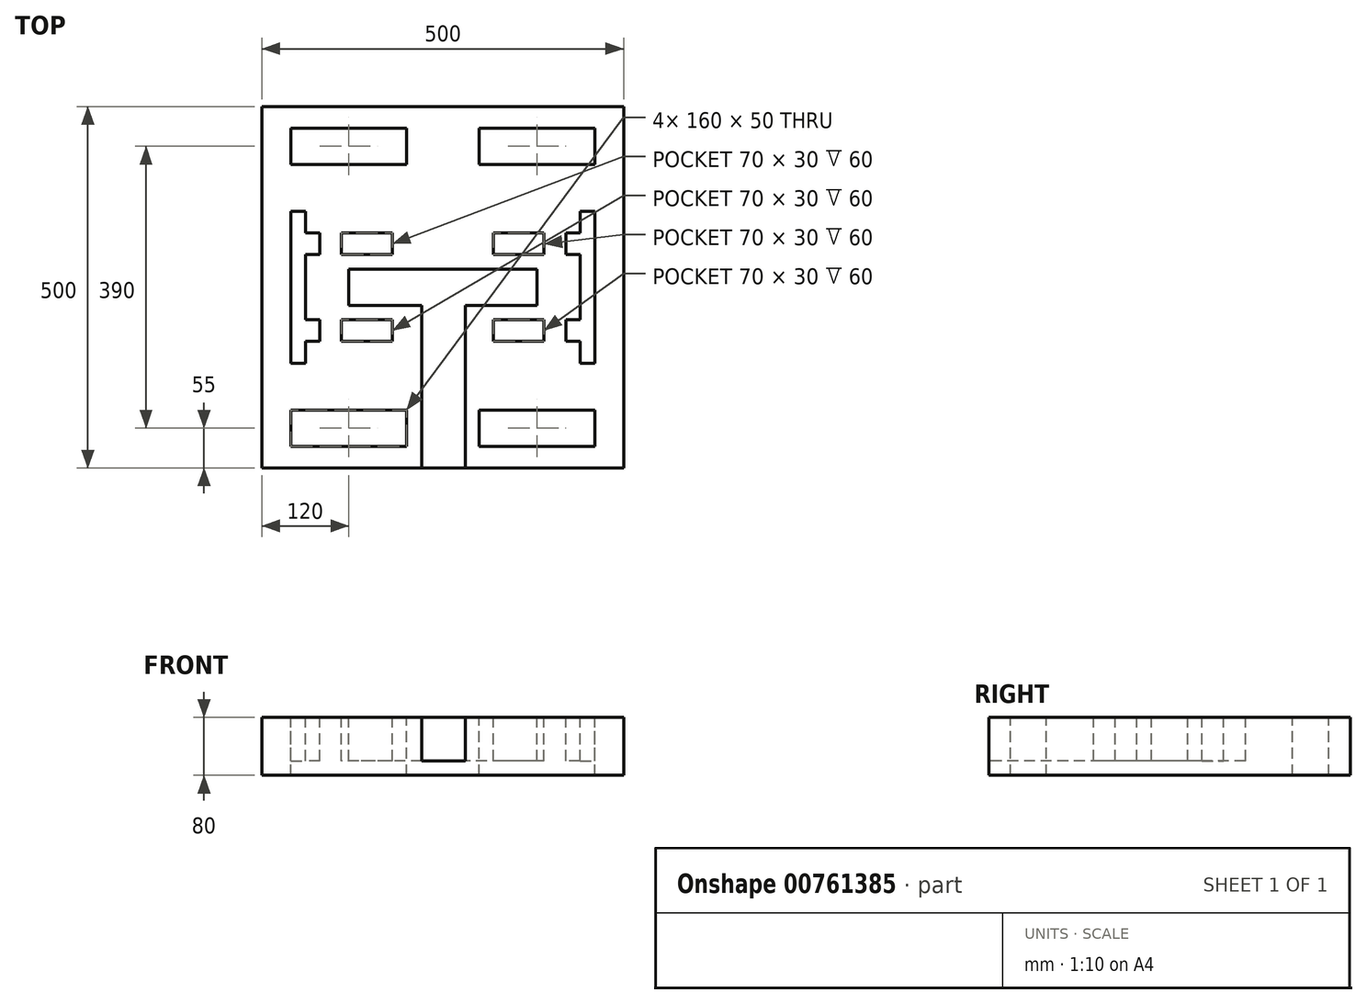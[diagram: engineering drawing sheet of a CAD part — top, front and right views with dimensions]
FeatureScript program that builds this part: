
annotation { "Feature Type Name" : "Feature", "Feature Type Description" : "" }
export const myFeature = defineFeature(function(context is Context, id is Id, definition is map)
    precondition{}
    {
        {
            var Q0;
            Q0=qCreatedBy(makeId("Top.planeOp"),FACE);
            var sketch = newSketch(context, id + "F0", { "sketchPlane" : qUnion([Q0])});
            skLineSegment(sketch, "E0.bottom", {"start": v(-250, 250) * mm, "end": v(250, 250) * mm});
            skLineSegment(sketch, "E0.top", {"start": v(-250, -250) * mm, "end": v(250, -250) * mm});
            skLineSegment(sketch, "E0.left", {"start": v(-250, 250) * mm, "end": v(-250, -250) * mm});
            skLineSegment(sketch, "E0.right", {"start": v(250, 250) * mm, "end": v(250, -250) * mm});
            skPoint(sketch, "E0.middle", {"position": v(0, 0) * mm});
            skSolve(sketch);
        }
        {
            var Q0;
            Q0=makeQuery(id+"F0.imprint","IMPRINT",FACE,{"disambiguationData":[TD([[makeQuery(id+"F0.imprint","IMPRINT",EDGE,{"derivedFrom":sQuery(id+"F0.wireOp",EDGE,"E0.bottom")}),-1.0]])]});
            extrude(context, id + "F1", {"entities" : qUnion([Q0]), "depth" : 80 * mm, "offsetDistance" : 25 * mm});
        }
        {
            var Q0;
            Q0=makeQuery(id+"F1.opExtrude","CAP_FACE",FACE,{"disambiguationData":[OSD([sQuery(id+"F0.wireOp",EDGE,"E0.bottom"),sQuery(id+"F0.wireOp",EDGE,"E0.top"),sQuery(id+"F0.wireOp",EDGE,"E0.left"),sQuery(id+"F0.wireOp",EDGE,"E0.right")])],"isStart":false});
            var sketch = newSketch(context, id + "F2", { "sketchPlane" : qUnion([Q0])});
            skLineSegment(sketch, "E1.bottom", {"start": v(-210, 105) * mm, "end": v(210, 105) * mm});
            skLineSegment(sketch, "E1.top", {"start": v(-210, -105) * mm, "end": v(210, -105) * mm});
            skLineSegment(sketch, "E1.left", {"start": v(-210, 105) * mm, "end": v(-210, -105) * mm});
            skLineSegment(sketch, "E1.right", {"start": v(210, 105) * mm, "end": v(210, -105) * mm});
            skPoint(sketch, "E1.middle", {"position": v(0, 0) * mm});
            skLineSegment(sketch, "E2", {"start": v(-190, 105) * mm, "end": v(-190, -105) * mm});
            skLineSegment(sketch, "E3", {"start": v(190, 105) * mm, "end": v(190, -105) * mm});
            skLineSegment(sketch, "E4", {"start": v(190, 75) * mm, "end": v(-190, 75) * mm});
            skLineSegment(sketch, "E5", {"start": v(190, -75) * mm, "end": v(-190, -75) * mm});
            skLineSegment(sketch, "E6", {"start": v(190, -45) * mm, "end": v(-190, -45) * mm});
            skLineSegment(sketch, "E7", {"start": v(190, 45) * mm, "end": v(-190, 45) * mm});
            skLineSegment(sketch, "E8", {"start": v(-170, 105) * mm, "end": v(-170, -105) * mm});
            skLineSegment(sketch, "E9", {"start": v(170, 105) * mm, "end": v(170, -105) * mm});
            skLineSegment(sketch, "E10", {"start": v(0, 0) * mm, "end": v(0, 105) * mm, "construction": true});
            skLineSegment(sketch, "E11", {"start": v(0, 0) * mm, "end": v(0, -105) * mm, "construction": true});
            skLineSegment(sketch, "E12", {"start": v(0, 0) * mm, "end": v(-170, 0) * mm, "construction": true});
            skLineSegment(sketch, "E13", {"start": v(0, 0) * mm, "end": v(170, 0) * mm, "construction": true});
            skLineSegment(sketch, "E14", {"start": v(70, -45) * mm, "end": v(70, 45) * mm});
            skLineSegment(sketch, "E15", {"start": v(-70, -45) * mm, "end": v(-70, 45) * mm});
            skLineSegment(sketch, "E16", {"start": v(-70, 45) * mm, "end": v(-70, 75) * mm});
            skLineSegment(sketch, "E17", {"start": v(-70, -45) * mm, "end": v(-70, -75) * mm});
            skLineSegment(sketch, "E18", {"start": v(-140, -45) * mm, "end": v(-140, -75) * mm});
            skLineSegment(sketch, "E19", {"start": v(-140, 75) * mm, "end": v(-140, 45) * mm});
            skLineSegment(sketch, "E20", {"start": v(-130, 45) * mm, "end": v(-130, -45) * mm});
            skLineSegment(sketch, "E21", {"start": v(140, 75) * mm, "end": v(140, 45) * mm});
            skPoint(sketch, "E21.endSnap0", {"position": v(0, 45) * mm});
            skLineSegment(sketch, "E22", {"start": v(140, -45) * mm, "end": v(140, -75) * mm});
            skLineSegment(sketch, "E23", {"start": v(70, -45) * mm, "end": v(70, -75) * mm});
            skLineSegment(sketch, "E24", {"start": v(70, 45) * mm, "end": v(70, 75) * mm});
            skLineSegment(sketch, "E25", {"start": v(130, 45) * mm, "end": v(130, -45) * mm});
            skLineSegment(sketch, "E26", {"start": v(-130, 25) * mm, "end": v(-70, 25) * mm});
            skLineSegment(sketch, "E27", {"start": v(-70, -25) * mm, "end": v(-130, -25) * mm});
            skLineSegment(sketch, "E28", {"start": v(70, 25) * mm, "end": v(130, 25) * mm});
            skLineSegment(sketch, "E29", {"start": v(70, -25) * mm, "end": v(130, -25) * mm});
            skLineSegment(sketch, "E30", {"start": v(-70, 25) * mm, "end": v(70, 25) * mm});
            skLineSegment(sketch, "E31", {"start": v(70, -25) * mm, "end": v(-70, -25) * mm});
            skSolve(sketch);
        }
        {
            var Q0;
            {var subQ4=sQuery(id+"F2.wireOp",EDGE,"E1.left");Q0=makeQuery(id+"F2.imprint","IMPRINT",FACE,{"disambiguationData":[TD([[makeQuery(id+"F2.imprint","IMPRINT",EDGE,{"derivedFrom":subQ4}),1.0]])]});}
            var Q1;
            {var subQ0=sQuery(id+"F2.wireOp",EDGE,"E4");var subQ1=sQuery(id+"F2.wireOp",EDGE,"E2");var subQ2=makeQuery(id+"F2.imprint","INTERSECT",VERTEX,{"derivedFrom":[subQ1,subQ0]});Q1=makeQuery(id+"F2.imprint","IMPRINT",FACE,{"disambiguationData":[TD([[makeQuery(id+"F2.imprint","IMPRINT",EDGE,{"disambiguationData":[TD([[subQ2,-1.0]])],"derivedFrom":subQ1}),1.0]])]});}
            var Q2;
            {var subQ0=sQuery(id+"F2.wireOp",EDGE,"E5");var subQ1=sQuery(id+"F2.wireOp",EDGE,"E2");var subQ2=makeQuery(id+"F2.imprint","INTERSECT",VERTEX,{"derivedFrom":[subQ1,subQ0]});Q2=makeQuery(id+"F2.imprint","IMPRINT",FACE,{"disambiguationData":[TD([[makeQuery(id+"F2.imprint","IMPRINT",EDGE,{"disambiguationData":[TD([[subQ2,1.0]])],"derivedFrom":subQ1}),1.0]])]});}
            var Q3;
            {var subQ0=sQuery(id+"F2.wireOp",EDGE,"E16");Q3=makeQuery(id+"F2.imprint","IMPRINT",FACE,{"disambiguationData":[TD([[makeQuery(id+"F2.imprint","IMPRINT",EDGE,{"derivedFrom":subQ0}),1.0]])]});}
            var Q4;
            {var subQ3=sQuery(id+"F2.wireOp",EDGE,"E17");Q4=makeQuery(id+"F2.imprint","IMPRINT",FACE,{"disambiguationData":[TD([[makeQuery(id+"F2.imprint","IMPRINT",EDGE,{"derivedFrom":subQ3}),-1.0]])]});}
            var Q5;
            {var subQ3=sQuery(id+"F2.wireOp",EDGE,"E21");Q5=makeQuery(id+"F2.imprint","IMPRINT",FACE,{"disambiguationData":[TD([[makeQuery(id+"F2.imprint","IMPRINT",EDGE,{"derivedFrom":subQ3}),-1.0]])]});}
            var Q6;
            {var subQ3=sQuery(id+"F2.wireOp",EDGE,"E22");Q6=makeQuery(id+"F2.imprint","IMPRINT",FACE,{"disambiguationData":[TD([[makeQuery(id+"F2.imprint","IMPRINT",EDGE,{"derivedFrom":subQ3}),-1.0]])]});}
            var Q7;
            {var subQ0=sQuery(id+"F2.wireOp",EDGE,"E4");var subQ1=sQuery(id+"F2.wireOp",EDGE,"E3");var subQ2=makeQuery(id+"F2.imprint","INTERSECT",VERTEX,{"derivedFrom":[subQ1,subQ0]});Q7=makeQuery(id+"F2.imprint","IMPRINT",FACE,{"disambiguationData":[TD([[makeQuery(id+"F2.imprint","IMPRINT",EDGE,{"disambiguationData":[TD([[subQ2,-1.0]])],"derivedFrom":subQ1}),-1.0]])]});}
            var Q8;
            {var subQ4=sQuery(id+"F2.wireOp",EDGE,"E1.right");Q8=makeQuery(id+"F2.imprint","IMPRINT",FACE,{"disambiguationData":[TD([[makeQuery(id+"F2.imprint","IMPRINT",EDGE,{"derivedFrom":subQ4}),-1.0]])]});}
            var Q9;
            {var subQ0=sQuery(id+"F2.wireOp",EDGE,"E5");var subQ1=sQuery(id+"F2.wireOp",EDGE,"E3");var subQ2=makeQuery(id+"F2.imprint","INTERSECT",VERTEX,{"derivedFrom":[subQ1,subQ0]});Q9=makeQuery(id+"F2.imprint","IMPRINT",FACE,{"disambiguationData":[TD([[makeQuery(id+"F2.imprint","IMPRINT",EDGE,{"disambiguationData":[TD([[subQ2,1.0]])],"derivedFrom":subQ1}),-1.0]])]});}
            var Q10;
            {var subQ0=sQuery(id+"F2.wireOp",EDGE,"E26");Q10=makeQuery(id+"F2.imprint","IMPRINT",FACE,{"disambiguationData":[TD([[makeQuery(id+"F2.imprint","IMPRINT",EDGE,{"derivedFrom":subQ0}),-1.0]])]});}
            var Q11;
            {var subQ0=sQuery(id+"F2.wireOp",EDGE,"E30");Q11=makeQuery(id+"F2.imprint","IMPRINT",FACE,{"disambiguationData":[TD([[makeQuery(id+"F2.imprint","IMPRINT",EDGE,{"derivedFrom":subQ0}),-1.0]])]});}
            var Q12;
            {var subQ0=sQuery(id+"F2.wireOp",EDGE,"E28");Q12=makeQuery(id+"F2.imprint","IMPRINT",FACE,{"disambiguationData":[TD([[makeQuery(id+"F2.imprint","IMPRINT",EDGE,{"derivedFrom":subQ0}),-1.0]])]});}
            extrude(context, id + "F3", {"entities" : qUnion([Q0, Q1, Q2, Q3, Q4, Q5, Q6, Q7, Q8, Q9, Q10, Q11, Q12]), "operationType" : NewBodyOperationType.REMOVE, "oppositeDirection" : true, "depth" : 60 * mm, "offsetDistance" : 25 * mm});
        }
        {
            var Q0;
            Q0=makeQuery(id+"F1.opExtrude","CAP_FACE",FACE,{"disambiguationData":[OSD([sQuery(id+"F0.wireOp",EDGE,"E0.bottom"),sQuery(id+"F0.wireOp",EDGE,"E0.top"),sQuery(id+"F0.wireOp",EDGE,"E0.left"),sQuery(id+"F0.wireOp",EDGE,"E0.right")])],"isStart":false});
            var sketch = newSketch(context, id + "F4", { "sketchPlane" : qUnion([Q0])});
            skLineSegment(sketch, "E32", {"start": v(0, 250) * mm, "end": v(0, 0) * mm, "construction": true});
            skLineSegment(sketch, "E33", {"start": v(0, 0) * mm, "end": v(-250, 0) * mm, "construction": true});
            skLineSegment(sketch, "E34", {"start": v(250, 0) * mm, "end": v(0, 0) * mm, "construction": true});
            skLineSegment(sketch, "E35", {"start": v(0, 0) * mm, "end": v(0, -250) * mm, "construction": true});
            skLineSegment(sketch, "E36", {"start": v(-210, 125) * mm, "end": v(210, 125) * mm, "construction": true});
            skLineSegment(sketch, "E37", {"start": v(-210, -125) * mm, "end": v(210, -125) * mm, "construction": true});
            skLineSegment(sketch, "E38", {"start": v(-210, -220) * mm, "end": v(210, -220) * mm});
            skLineSegment(sketch, "E39", {"start": v(-210, 220) * mm, "end": v(210, 220) * mm});
            skLineSegment(sketch, "E40", {"start": v(-210, 170) * mm, "end": v(210, 170) * mm});
            skLineSegment(sketch, "E41", {"start": v(-210, -170) * mm, "end": v(210, -170) * mm});
            skLineSegment(sketch, "E42", {"start": v(-50, -170) * mm, "end": v(-50, -220) * mm});
            skLineSegment(sketch, "E43", {"start": v(50, -170) * mm, "end": v(50, -220) * mm});
            skLineSegment(sketch, "E44", {"start": v(-50, 220) * mm, "end": v(-50, 170) * mm});
            skLineSegment(sketch, "E45", {"start": v(50, 220) * mm, "end": v(50, 170) * mm});
            skLineSegment(sketch, "E46", {"start": v(-210, 220) * mm, "end": v(-210, 170) * mm});
            skLineSegment(sketch, "E47", {"start": v(210, 220) * mm, "end": v(210, 170) * mm});
            skLineSegment(sketch, "E48", {"start": v(210, -170) * mm, "end": v(210, -220) * mm});
            skLineSegment(sketch, "E49", {"start": v(-210, -170) * mm, "end": v(-210, -220) * mm});
            skSolve(sketch);
        }
        {
            var Q0;
            {var subQ2=sQuery(id+"F4.wireOp",EDGE,"E44");Q0=makeQuery(id+"F4.imprint","IMPRINT",FACE,{"disambiguationData":[TD([[makeQuery(id+"F4.imprint","IMPRINT",EDGE,{"derivedFrom":subQ2}),-1.0]])]});}
            var Q1;
            {var subQ2=sQuery(id+"F4.wireOp",EDGE,"E45");Q1=makeQuery(id+"F4.imprint","IMPRINT",FACE,{"disambiguationData":[TD([[makeQuery(id+"F4.imprint","IMPRINT",EDGE,{"derivedFrom":subQ2}),1.0]])]});}
            var Q2;
            {var subQ2=sQuery(id+"F4.wireOp",EDGE,"E43");Q2=makeQuery(id+"F4.imprint","IMPRINT",FACE,{"disambiguationData":[TD([[makeQuery(id+"F4.imprint","IMPRINT",EDGE,{"derivedFrom":subQ2}),1.0]])]});}
            var Q3;
            {var subQ2=sQuery(id+"F4.wireOp",EDGE,"E42");Q3=makeQuery(id+"F4.imprint","IMPRINT",FACE,{"disambiguationData":[TD([[makeQuery(id+"F4.imprint","IMPRINT",EDGE,{"derivedFrom":subQ2}),-1.0]])]});}
            extrude(context, id + "F5", {"entities" : qUnion([Q0, Q1, Q2, Q3]), "operationType" : NewBodyOperationType.REMOVE, "oppositeDirection" : true, "depth" : 190 * mm, "offsetDistance" : 25 * mm});
        }
        {
            var Q0;
            Q0=makeQuery(id+"F1.opExtrude","CAP_FACE",FACE,{"disambiguationData":[OSD([sQuery(id+"F0.wireOp",EDGE,"E0.bottom"),sQuery(id+"F0.wireOp",EDGE,"E0.top"),sQuery(id+"F0.wireOp",EDGE,"E0.left"),sQuery(id+"F0.wireOp",EDGE,"E0.right")])],"isStart":false});
            var sketch = newSketch(context, id + "F6", { "sketchPlane" : qUnion([Q0])});
            skLineSegment(sketch, "E50", {"start": v(31.13, -25) * mm, "end": v(31.13, -250) * mm});
            skLineSegment(sketch, "E51", {"start": v(-28.87, -25) * mm, "end": v(-28.87, -250) * mm});
            skLineSegment(sketch, "E52", {"start": v(-28.87, -250) * mm, "end": v(31.13, -250) * mm});
            skSolve(sketch);
        }
        {
            var Q0;
            {var subQ0=sQuery(id+"F6.wireOp",EDGE,"E50");Q0=makeQuery(id+"F6.imprint","IMPRINT",FACE,{"disambiguationData":[TD([[makeQuery(id+"F6.imprint","IMPRINT",EDGE,{"derivedFrom":subQ0}),-1.0]])]});}
            extrude(context, id + "F7", {"entities" : qUnion([Q0]), "operationType" : NewBodyOperationType.REMOVE, "oppositeDirection" : true, "depth" : 60 * mm, "offsetDistance" : 25 * mm});
        }
    });
